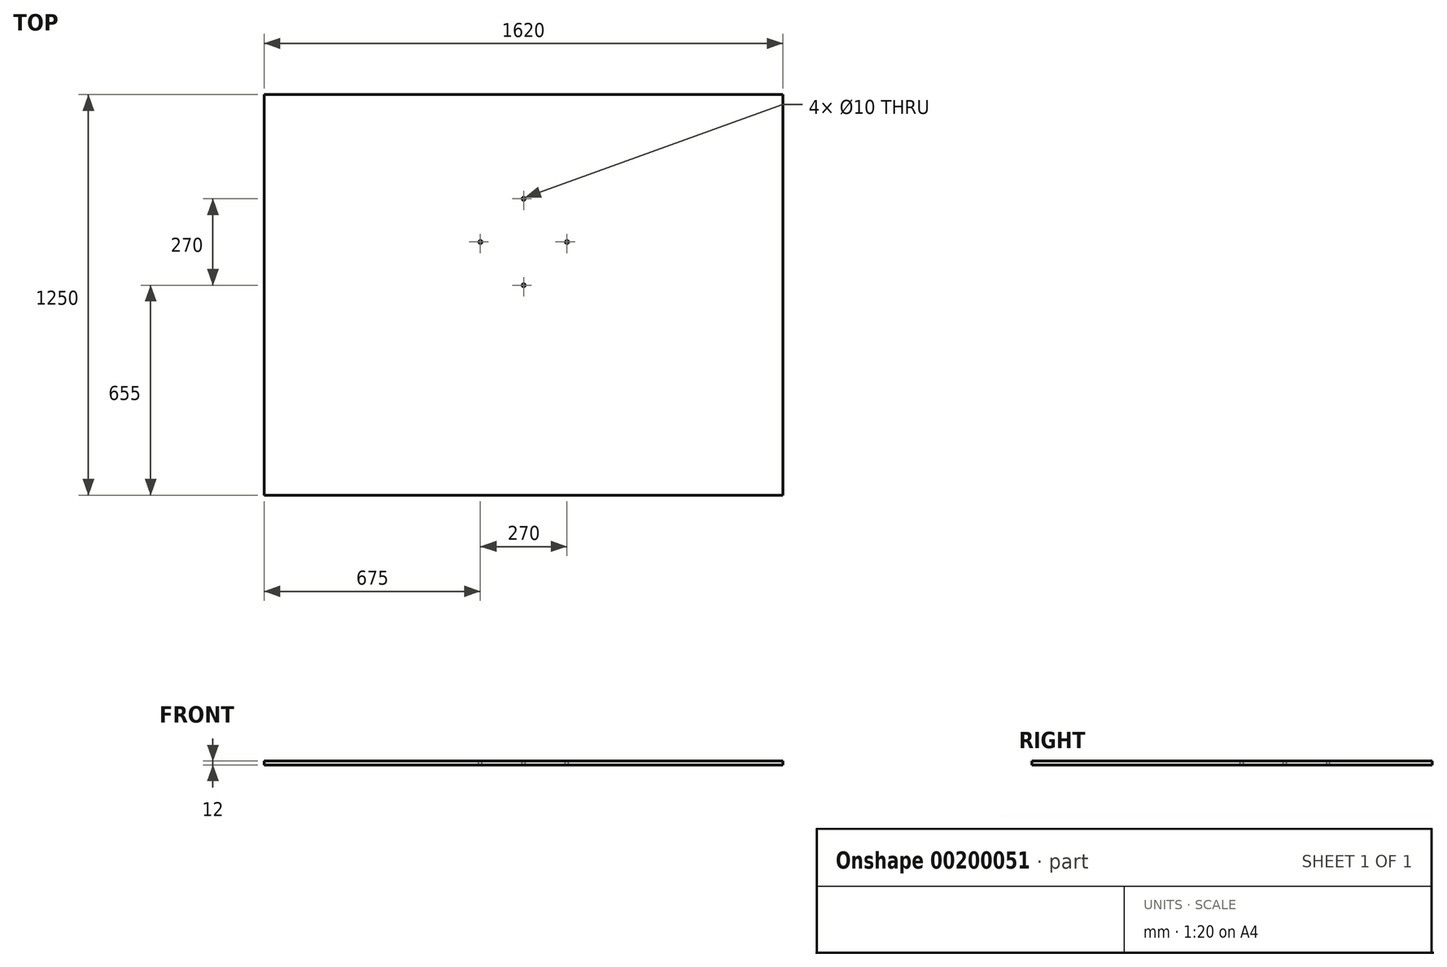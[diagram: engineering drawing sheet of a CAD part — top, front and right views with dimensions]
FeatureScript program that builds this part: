
annotation { "Feature Type Name" : "Feature", "Feature Type Description" : "" }
export const myFeature = defineFeature(function(context is Context, id is Id, definition is map)
    precondition{}
    {
        {
            var Q0;
            Q0=qCreatedBy(makeId("Top.planeOp"),FACE);
            var sketch = newSketch(context, id + "F0", { "sketchPlane" : qUnion([Q0])});
            skLineSegment(sketch, "E0.bottom", {"start": v(810, -625) * mm, "end": v(-810, -625) * mm});
            skLineSegment(sketch, "E0.top", {"start": v(810, 625) * mm, "end": v(-810, 625) * mm});
            skLineSegment(sketch, "E0.left", {"start": v(810, -625) * mm, "end": v(810, 625) * mm});
            skLineSegment(sketch, "E0.right", {"start": v(-810, -625) * mm, "end": v(-810, 625) * mm});
            skPoint(sketch, "E0.middle", {"position": v(0, 0) * mm});
            skSolve(sketch);
        }
        {
            var Q0;
            Q0 = qSketchRegion(id + "F0", true);
            extrude(context, id + "F1", {"entities" : qUnion([Q0]), "depth" : 12 * mm});
        }
        {
            var Q0;
            Q0=makeQuery(id+"F1.opExtrude","CAP_FACE",FACE,{"disambiguationData":[OSD([sQuery(id+"F0.wireOp",EDGE,"E0.bottom"),sQuery(id+"F0.wireOp",EDGE,"E0.top"),sQuery(id+"F0.wireOp",EDGE,"E0.left"),sQuery(id+"F0.wireOp",EDGE,"E0.right")])],"isStart":false});
            var sketch = newSketch(context, id + "F2", { "sketchPlane" : qUnion([Q0])});
            skLineSegment(sketch, "E1", {"start": v(0, 625) * mm, "end": v(0, 300) * mm, "construction": true});
            skPoint(sketch, "E1.endSnap0", {"position": v(0, 625) * mm});
            skCircle(sketch, "E2", {"center": v(0, 300) * mm, "radius": 5 * mm});
            skCircle(sketch, "E3", {"center": v(0, 30) * mm, "radius": 5 * mm});
            skLineSegment(sketch, "E4", {"start": v(-135, 165) * mm, "end": v(135, 165) * mm, "construction": true});
            skCircle(sketch, "E5", {"center": v(-135, 165) * mm, "radius": 5 * mm});
            skCircle(sketch, "E6.MirrorC", {"center": v(135, 165) * mm, "radius": 5 * mm});
            skLineSegment(sketch, "E7", {"start": v(0, 300) * mm, "end": v(0, 30) * mm, "construction": true});
            skPoint(sketch, "E8", {"position": v(0, 165) * mm});
            skSolve(sketch);
        }
        {
            var Q0;
            Q0 = qSketchRegion(id + "F2", true);
            extrude(context, id + "F3", {"entities" : qUnion([Q0]), "operationType" : NewBodyOperationType.REMOVE, "endBound" : BoundingType.THROUGH_ALL, "oppositeDirection" : true, "depth" : 25 * mm});
        }
    });
